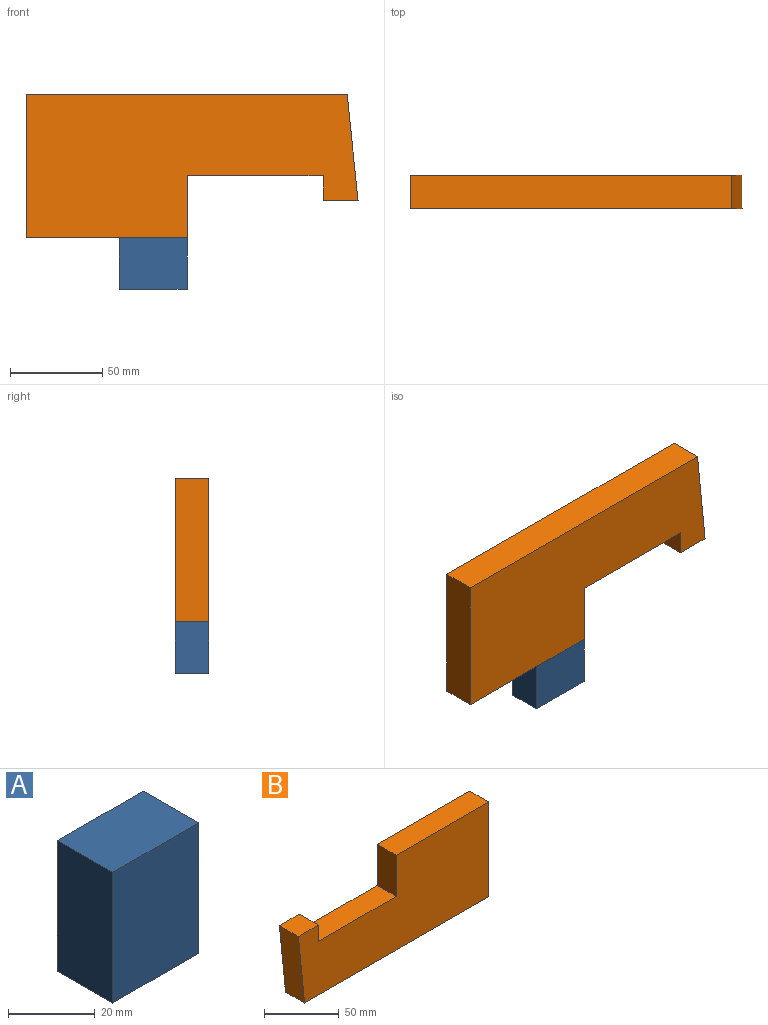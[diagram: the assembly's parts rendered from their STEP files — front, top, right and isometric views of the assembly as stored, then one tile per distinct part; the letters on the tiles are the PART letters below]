
ASSEMBLY  parts=2 mates=1
PART A: 6 faces, bbox 28x18x36.9 mm
  f0: plane 28.03x18mm, normal (0,0,-1), area 504.5mm2, adj f1,f3,f4,f5
  f1: plane 36.88x18mm, normal (1,0,0), area 663.9mm2, adj f0,f2,f4,f5
  f2: plane 28.03x18mm, normal (0,0,1), area 504.5mm2, adj f1,f3,f4,f5
  f3: plane 36.88x18mm, normal (-1,0,0), area 663.9mm2, adj f0,f2,f4,f5
  f4: plane 36.88x28.03mm, normal (0,-1,0), area 1033.8mm2, adj f0,f1,f2,f3
  f5: plane 36.88x28.03mm, normal (0,1,0), area 1033.8mm2, adj f0,f1,f2,f3
PART B: 10 faces, bbox 180.4x18x77.8 mm
  f0: plane 18.96x18mm, normal (0,0,1), area 341.2mm2, adj f1,f7,f8,f9
  f1: plane 57.43x18mm, normal (-0.99,0,-0.1), area 1039.1mm2, adj f0,f2,f8,f9
  f2: plane 174.52x18mm, normal (0,0,-1), area 3141.3mm2, adj f1,f3,f8,f9
  f3: plane 77.78x18mm, normal (1,0,0), area 1400mm2, adj f2,f4,f8,f9
  f4: plane 87.54x18mm, normal (0,0,1), area 1575.7mm2, adj f3,f5,f8,f9
  f5: plane 33.73x18mm, normal (-1,0,0), area 607.2mm2, adj f4,f6,f8,f9
  f6: plane 73.88x18mm, normal (0,0,1), area 1329.8mm2, adj f5,f7,f8,f9
  f7: plane 18x13.38mm, normal (1,0,0), area 240.9mm2, adj f0,f6,f8,f9
  f8: plane 180.37x77.78mm, normal (0,-1,0), area 10983.3mm2, adj f0,f1,f2,f3,f4,f5,f6,f7
  f9: plane 180.37x77.78mm, normal (0,1,0), area 10983.3mm2, adj f0,f1,f2,f3,f4,f5,f6,f7
PLACE A rot(axis=(0.71,0,-0.71),180deg) t=(119.8,95.39,56.85)mm
PLACE B rot(axis=(0,-1,0),180deg) t=(-3.1,113.39,137.93)mm
MATE fastened A.f3 <-> B.f4  axis (0,0,1) through (-11.19,104.39,92.35)mm
